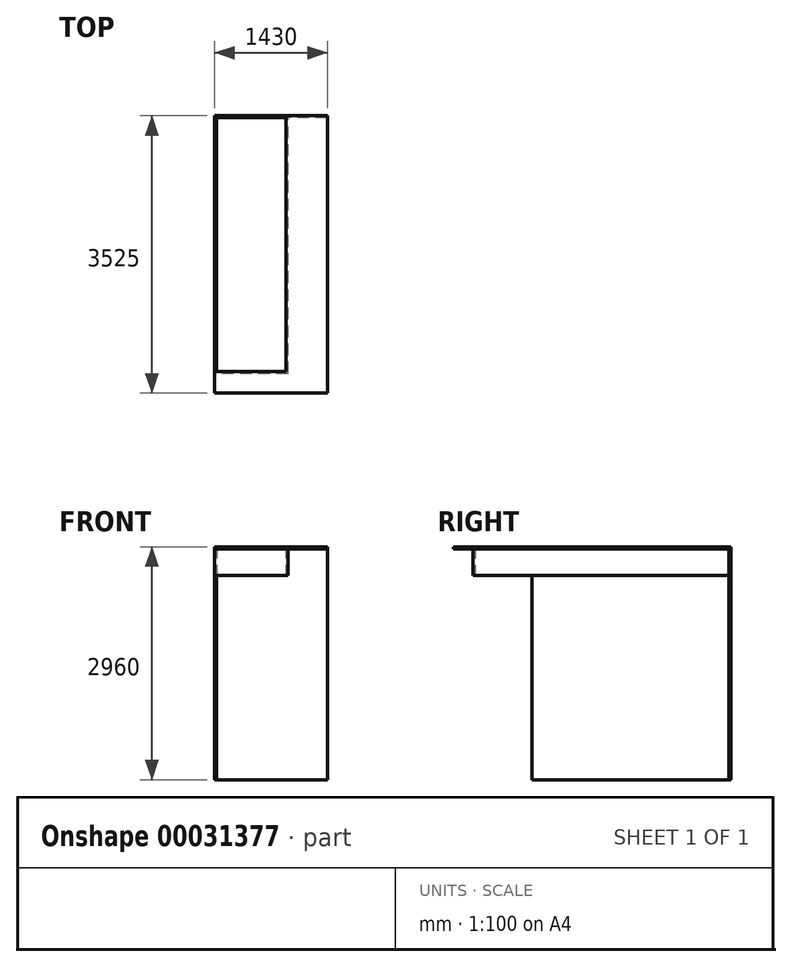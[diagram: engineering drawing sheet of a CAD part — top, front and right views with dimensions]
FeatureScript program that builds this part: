
annotation { "Feature Type Name" : "Feature", "Feature Type Description" : "" }
export const myFeature = defineFeature(function(context is Context, id is Id, definition is map)
    precondition{}
    {
        {
            var Q0;
            Q0=qCreatedBy(makeId("Front.planeOp"),FACE);
            cPlane(context, id + "F0", {"entities" : qUnion([Q0]), "cplaneType" : CPlaneType.OFFSET, "offset" : 3225 * mm, "width" : 150 * mm, "height" : 150 * mm});
        }
        {
            var Q0;
            Q0=qCreatedBy(makeId("Right.planeOp"),FACE);
            cPlane(context, id + "F1", {"entities" : qUnion([Q0]), "cplaneType" : CPlaneType.OFFSET, "offset" : 880 * mm, "width" : 150 * mm, "height" : 150 * mm});
        }
        {
            var Q0;
            Q0=qCreatedBy(makeId("Top.planeOp"),FACE);
            cPlane(context, id + "F2", {"entities" : qUnion([Q0]), "cplaneType" : CPlaneType.OFFSET, "offset" : 2960 * mm, "width" : 150 * mm, "height" : 150 * mm});
        }
        {
            var Q0;
            Q0=qCreatedBy(id+"F1.planeOp",FACE);
            var sketch = newSketch(context, id + "F3", { "sketchPlane" : qUnion([Q0])});
            skLineSegment(sketch, "E0.bottom", {"start": v(-3225, 2960) * mm, "end": v(0, 2960) * mm});
            skLineSegment(sketch, "E0.top", {"start": v(-3225, 2598) * mm, "end": v(0, 2598) * mm});
            skLineSegment(sketch, "E0.left", {"start": v(-3225, 2960) * mm, "end": v(-3225, 2598) * mm});
            skLineSegment(sketch, "E0.right", {"start": v(0, 2960) * mm, "end": v(0, 2598) * mm});
            skSolve(sketch);
        }
        {
            var Q0;
            Q0=makeQuery(id+"F3.imprint","IMPRINT",FACE,{"disambiguationData":[TD([[makeQuery(id+"F3.imprint","IMPRINT",EDGE,{"derivedFrom":sQuery(id+"F3.wireOp",EDGE,"E0.bottom")}),-1.0]])]});
            extrude(context, id + "F4", {"entities" : qUnion([Q0]), "depth" : 25 * mm});
        }
        {
            var Q0;
            Q0=qCreatedBy(id+"F0.planeOp",FACE);
            var sketch = newSketch(context, id + "F5", { "sketchPlane" : qUnion([Q0])});
            skLineSegment(sketch, "E1.bottom", {"start": v(905, 2960) * mm, "end": v(0, 2960) * mm});
            skLineSegment(sketch, "E1.top", {"start": v(905, 2598) * mm, "end": v(0, 2598) * mm});
            skLineSegment(sketch, "E1.left", {"start": v(905, 2960) * mm, "end": v(905, 2598) * mm});
            skLineSegment(sketch, "E1.right", {"start": v(0, 2960) * mm, "end": v(0, 2598) * mm});
            skSolve(sketch);
        }
        {
            var Q0;
            Q0=makeQuery(id+"F5.imprint","IMPRINT",FACE,{"disambiguationData":[TD([[makeQuery(id+"F5.imprint","IMPRINT",EDGE,{"derivedFrom":sQuery(id+"F5.wireOp",EDGE,"E1.bottom")}),1.0]])]});
            extrude(context, id + "F6", {"entities" : qUnion([Q0]), "operationType" : NewBodyOperationType.ADD, "depth" : 25 * mm});
        }
        {
            var Q0;
            Q0=qCreatedBy(makeId("Right.planeOp"),FACE);
            var sketch = newSketch(context, id + "F7", { "sketchPlane" : qUnion([Q0])});
            skLineSegment(sketch, "E2.bottom", {"start": v(0, 0) * mm, "end": v(-2500, 0) * mm});
            skLineSegment(sketch, "E2.top", {"start": v(0, 2960) * mm, "end": v(-3250, 2960) * mm});
            skLineSegment(sketch, "E2.left", {"start": v(0, 0) * mm, "end": v(0, 2960) * mm});
            skLineSegment(sketch, "E2.right", {"start": v(-2500, 0) * mm, "end": v(-2500, 2598) * mm});
            skLineSegment(sketch, "E3", {"start": v(-3250, 2960) * mm, "end": v(-3250, 2598) * mm});
            skLineSegment(sketch, "E4", {"start": v(-3250, 2598) * mm, "end": v(-2500, 2598) * mm});
            skSolve(sketch);
        }
        {
            var Q0;
            Q0=makeQuery(id+"F7.imprint","IMPRINT",FACE,{"disambiguationData":[TD([[makeQuery(id+"F7.imprint","IMPRINT",EDGE,{"derivedFrom":sQuery(id+"F7.wireOp",EDGE,"E2.bottom")}),-1.0]])]});
            extrude(context, id + "F8", {"entities" : qUnion([Q0]), "operationType" : NewBodyOperationType.ADD, "oppositeDirection" : true, "depth" : 25 * mm});
        }
        {
            var Q0;
            Q0=qCreatedBy(makeId("Front.planeOp"),FACE);
            var sketch = newSketch(context, id + "F9", { "sketchPlane" : qUnion([Q0])});
            skLineSegment(sketch, "E5.bottom", {"start": v(-25, 0) * mm, "end": v(1405, 0) * mm});
            skLineSegment(sketch, "E5.top", {"start": v(-25, 2960) * mm, "end": v(1405, 2960) * mm});
            skLineSegment(sketch, "E5.left", {"start": v(-25, 0) * mm, "end": v(-25, 2960) * mm});
            skLineSegment(sketch, "E5.right", {"start": v(1405, 0) * mm, "end": v(1405, 2960) * mm});
            skSolve(sketch);
        }
        {
            var Q0;
            Q0=makeQuery(id+"F9.imprint","IMPRINT",FACE,{"disambiguationData":[TD([[makeQuery(id+"F9.imprint","IMPRINT",EDGE,{"derivedFrom":sQuery(id+"F9.wireOp",EDGE,"E5.bottom")}),1.0]])]});
            extrude(context, id + "F10", {"entities" : qUnion([Q0]), "operationType" : NewBodyOperationType.ADD, "oppositeDirection" : true, "depth" : 25 * mm});
        }
        {
            var Q0;
            Q0=makeQuery(id+"F10.boolean.opBoolean","MERGE",FACE,{"derivedFrom":[makeQuery(id+"F8.boolean.opBoolean","MERGE",FACE,{"derivedFrom":[makeQuery(id+"F6.boolean.opBoolean","MERGE",FACE,{"derivedFrom":[makeQuery(id+"F4.opExtrude","SWEPT_FACE",FACE,{"disambiguationData":[OSD([sQuery(id+"F3.wireOp",EDGE,"E0.bottom")])]}),makeQuery(id+"F6.opExtrude","SWEPT_FACE",FACE,{"disambiguationData":[OSD([sQuery(id+"F5.wireOp",EDGE,"E1.bottom")])]})]}),makeQuery(id+"F8.opExtrude","SWEPT_FACE",FACE,{"disambiguationData":[OSD([sQuery(id+"F7.wireOp",EDGE,"E2.top")])]})]}),makeQuery(id+"F10.opExtrude","SWEPT_FACE",FACE,{"disambiguationData":[OSD([sQuery(id+"F9.wireOp",EDGE,"E5.top")])]})]});
            var sketch = newSketch(context, id + "F11", { "sketchPlane" : qUnion([Q0])});
            skLineSegment(sketch, "E6", {"start": v(905, 25) * mm, "end": v(1405, 25) * mm});
            skLineSegment(sketch, "E7", {"start": v(1405, 25) * mm, "end": v(1405, -3500) * mm});
            skLineSegment(sketch, "E8", {"start": v(1405, -3500) * mm, "end": v(-25, -3500) * mm});
            skLineSegment(sketch, "E9", {"start": v(-25, -3500) * mm, "end": v(-25, -3250) * mm});
            skLineSegment(sketch, "E10", {"start": v(-25, -3250) * mm, "end": v(905, -3250) * mm});
            skLineSegment(sketch, "E11", {"start": v(905, -3250) * mm, "end": v(905, 25) * mm});
            skSolve(sketch);
        }
        {
            var Q0;
            Q0=makeQuery(id+"F11.imprint","IMPRINT",FACE,{"disambiguationData":[TD([[makeQuery(id+"F11.imprint","IMPRINT",EDGE,{"derivedFrom":sQuery(id+"F11.wireOp",EDGE,"E6")}),-1.0]])]});
            var Q1;
            {var subQ5=sQuery(id+"F11.wireOp",EDGE,"E8");Q1=makeQuery(id+"F11.imprint","IMPRINT",FACE,{"disambiguationData":[TD([[makeQuery(id+"F11.imprint","IMPRINT",EDGE,{"derivedFrom":subQ5}),-1.0]])]});}
            extrude(context, id + "F12", {"entities" : qUnion([Q0, Q1]), "operationType" : NewBodyOperationType.ADD, "oppositeDirection" : true, "depth" : 25 * mm});
        }
    });
